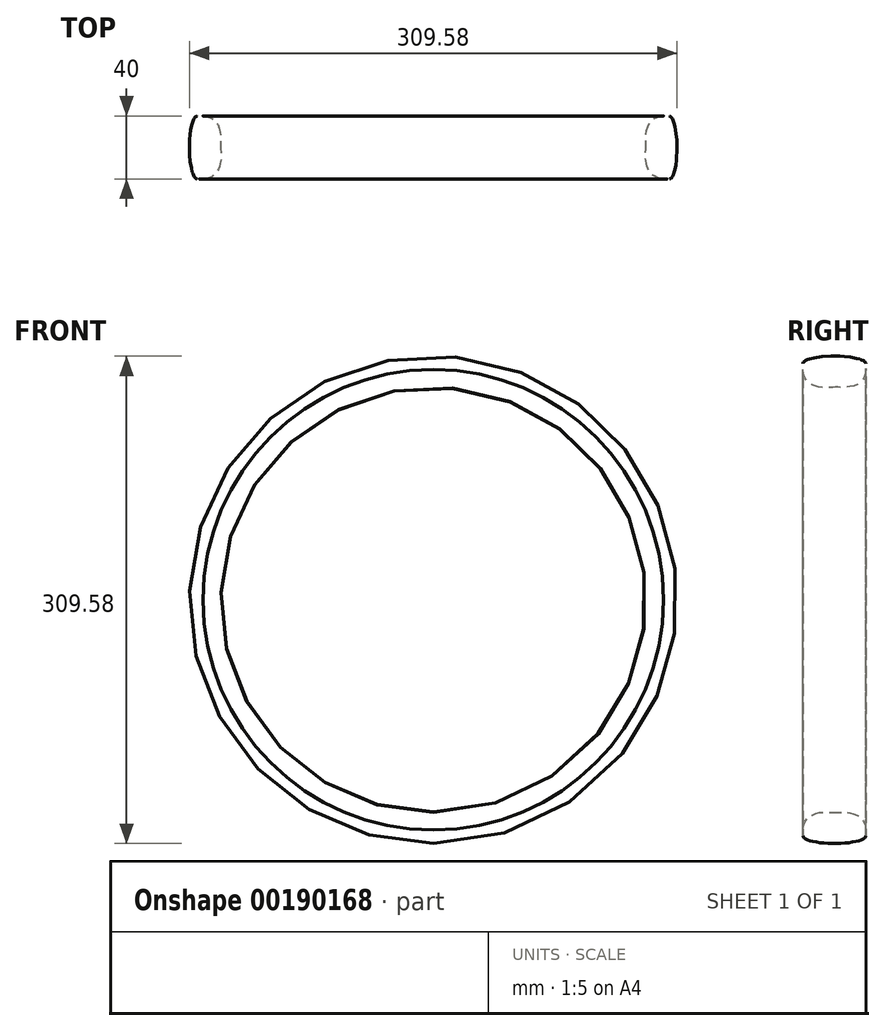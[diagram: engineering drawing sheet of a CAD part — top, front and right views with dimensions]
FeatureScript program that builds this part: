
annotation { "Feature Type Name" : "Feature", "Feature Type Description" : "" }
export const myFeature = defineFeature(function(context is Context, id is Id, definition is map)
    precondition{}
    {
        {
            var Q0;
            Q0=qCreatedBy(makeId("Right.planeOp"),FACE);
            var sketch = newSketch(context, id + "F0", { "sketchPlane" : qUnion([Q0])});
            skEllipticalArc(sketch, "E0", {});
            skLineSegment(sketch, "E1", {"start": v(20, 150) * mm, "end": v(20, 146.95) * mm});
            skLineSegment(sketch, "E2", {"start": v(-20, 150) * mm, "end": v(-20, 146.22) * mm});
            skPoint(sketch, "E3.orphan", {"position": v(-20, 137.5) * mm});
            skPoint(sketch, "E4.orphan", {"position": v(20, 137.5) * mm});
            skFitSpline(sketch, "E5", {"points": [v(-20, 146.22) * mm, v(-11.72, 135.67) * mm, v(0, 135.02) * mm, v(8.52, 135.18) * mm, v(20, 146.95) * mm], "startDerivative": vector(1.56, -68) * mm, "endDerivative": vector(0, 98.31) * mm});
            skLineSegment(sketch, "E6", {"start": v(-21.52, 0) * mm, "end": v(21.4, 0) * mm});
            const initialGuessF0  = {"E0": [0, 0.15, -1, 0, 0.02, 0.004792675245261658, 3.1415926535897927, 6.283185307179585]};
            skSetInitialGuess(sketch, initialGuessF0);
            skSolve(sketch);
        }
        {
            var Q0;
            Q0=makeQuery(id+"F0.imprint","IMPRINT",FACE,{"disambiguationData":[TD([[makeQuery(id+"F0.imprint","IMPRINT",EDGE,{"derivedFrom":sQuery(id+"F0.wireOp",EDGE,"E0")}),1.0]])]});
            var Q1;
            Q1=sQuery(id+"F0.wireOp",EDGE,"E6");
            revolve(context, id + "F1", {"entities" : qUnion([Q0]), "axis" : qUnion([Q1]), "revolveType" : RevolveType.FULL});
        }
    });
